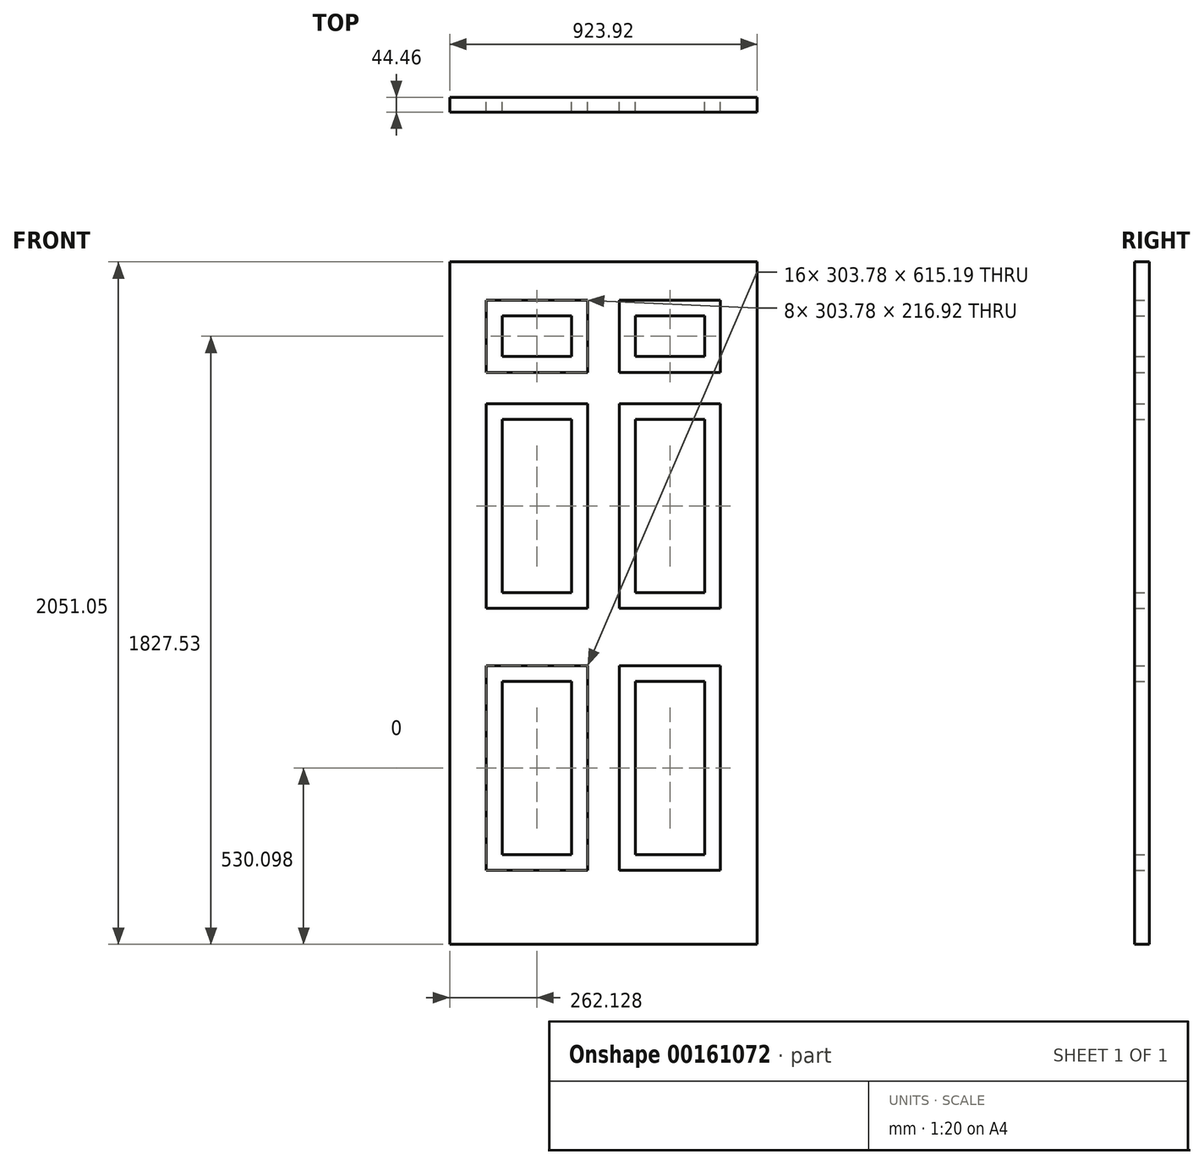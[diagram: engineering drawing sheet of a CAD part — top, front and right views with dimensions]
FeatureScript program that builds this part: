
annotation { "Feature Type Name" : "Feature", "Feature Type Description" : "" }
export const myFeature = defineFeature(function(context is Context, id is Id, definition is map)
    precondition{}
    {
        {
            var Q0;
            Q0=qCreatedBy(makeId("Front.planeOp"),FACE);
            var sketch = newSketch(context, id + "F0", { "sketchPlane" : qUnion([Q0])});
            skLineSegment(sketch, "E0.bottom", {"start": v(0, 0) * mm, "end": v(923.93, 0) * mm});
            skLineSegment(sketch, "E0.top", {"start": v(0, 2051.05) * mm, "end": v(923.92, 2051.05) * mm});
            skLineSegment(sketch, "E0.left", {"start": v(0, 0) * mm, "end": v(0, 2051.05) * mm});
            skLineSegment(sketch, "E0.right", {"start": v(923.93, 0) * mm, "end": v(923.92, 2051.05) * mm});
            skLineSegment(sketch, "E1.bottom", {"start": v(110.24, 222.5) * mm, "end": v(414.02, 222.5) * mm});
            skLineSegment(sketch, "E1.top", {"start": v(110.24, 837.7) * mm, "end": v(414.02, 837.7) * mm});
            skLineSegment(sketch, "E1.left", {"start": v(110.24, 222.5) * mm, "end": v(110.24, 837.7) * mm});
            skLineSegment(sketch, "E1.right", {"start": v(414.02, 222.5) * mm, "end": v(414.02, 837.7) * mm});
            skLineSegment(sketch, "E2.bottom", {"start": v(509.9, 222.5) * mm, "end": v(813.69, 222.5) * mm});
            skLineSegment(sketch, "E2.top", {"start": v(509.9, 837.7) * mm, "end": v(813.69, 837.7) * mm});
            skLineSegment(sketch, "E2.left", {"start": v(509.9, 222.5) * mm, "end": v(509.9, 837.7) * mm});
            skLineSegment(sketch, "E2.right", {"start": v(813.69, 222.5) * mm, "end": v(813.69, 837.7) * mm});
            skLineSegment(sketch, "E3.bottom", {"start": v(414.02, 1009.65) * mm, "end": v(110.24, 1009.65) * mm});
            skLineSegment(sketch, "E3.top", {"start": v(414.02, 1624.84) * mm, "end": v(110.24, 1624.84) * mm});
            skLineSegment(sketch, "E3.left", {"start": v(414.02, 1009.65) * mm, "end": v(414.02, 1624.84) * mm});
            skLineSegment(sketch, "E3.right", {"start": v(110.24, 1009.65) * mm, "end": v(110.24, 1624.84) * mm});
            skLineSegment(sketch, "E4.bottom", {"start": v(110.24, 1719.07) * mm, "end": v(414.02, 1719.07) * mm});
            skLineSegment(sketch, "E4.top", {"start": v(110.24, 1935.99) * mm, "end": v(414.02, 1935.99) * mm});
            skLineSegment(sketch, "E4.left", {"start": v(110.24, 1719.07) * mm, "end": v(110.24, 1935.99) * mm});
            skLineSegment(sketch, "E4.right", {"start": v(414.02, 1719.07) * mm, "end": v(414.02, 1935.99) * mm});
            skLineSegment(sketch, "E5.bottom", {"start": v(509.9, 1009.65) * mm, "end": v(813.69, 1009.65) * mm});
            skLineSegment(sketch, "E5.top", {"start": v(509.9, 1624.84) * mm, "end": v(813.69, 1624.84) * mm});
            skLineSegment(sketch, "E5.left", {"start": v(509.9, 1009.65) * mm, "end": v(509.9, 1624.84) * mm});
            skLineSegment(sketch, "E5.right", {"start": v(813.69, 1009.65) * mm, "end": v(813.69, 1624.84) * mm});
            skLineSegment(sketch, "E6.bottom", {"start": v(509.9, 1719.07) * mm, "end": v(813.69, 1719.07) * mm});
            skLineSegment(sketch, "E6.top", {"start": v(509.9, 1935.99) * mm, "end": v(813.69, 1935.99) * mm});
            skLineSegment(sketch, "E6.left", {"start": v(509.9, 1719.07) * mm, "end": v(509.9, 1935.99) * mm});
            skLineSegment(sketch, "E6.right", {"start": v(813.69, 1719.07) * mm, "end": v(813.69, 1935.99) * mm});
            skLineSegment(sketch, "E7.0", {"start": v(157.73, 1888.5) * mm, "end": v(366.52, 1888.5) * mm});
            skLineSegment(sketch, "E7.1", {"start": v(157.73, 1766.57) * mm, "end": v(157.73, 1888.5) * mm});
            skLineSegment(sketch, "E7.2", {"start": v(157.73, 1766.57) * mm, "end": v(366.52, 1766.57) * mm});
            skLineSegment(sketch, "E7.3", {"start": v(366.52, 1766.57) * mm, "end": v(366.52, 1888.5) * mm});
            skLineSegment(sketch, "E8.0", {"start": v(557.4, 1888.5) * mm, "end": v(766.2, 1888.5) * mm});
            skLineSegment(sketch, "E8.1", {"start": v(557.4, 1766.57) * mm, "end": v(557.4, 1888.5) * mm});
            skLineSegment(sketch, "E8.2", {"start": v(557.4, 1766.57) * mm, "end": v(766.2, 1766.57) * mm});
            skLineSegment(sketch, "E8.3", {"start": v(766.2, 1766.57) * mm, "end": v(766.2, 1888.5) * mm});
            skLineSegment(sketch, "E9.0", {"start": v(366.52, 1577.34) * mm, "end": v(157.73, 1577.34) * mm});
            skLineSegment(sketch, "E9.1", {"start": v(366.52, 1057.15) * mm, "end": v(366.52, 1577.34) * mm});
            skLineSegment(sketch, "E9.2", {"start": v(366.52, 1057.15) * mm, "end": v(157.73, 1057.15) * mm});
            skLineSegment(sketch, "E9.3", {"start": v(157.73, 1057.15) * mm, "end": v(157.73, 1577.34) * mm});
            skLineSegment(sketch, "E10.0", {"start": v(557.4, 1057.15) * mm, "end": v(557.4, 1577.34) * mm});
            skLineSegment(sketch, "E10.1", {"start": v(557.4, 1057.15) * mm, "end": v(766.2, 1057.15) * mm});
            skLineSegment(sketch, "E10.2", {"start": v(766.2, 1057.15) * mm, "end": v(766.2, 1577.34) * mm});
            skLineSegment(sketch, "E10.3", {"start": v(557.4, 1577.34) * mm, "end": v(766.2, 1577.34) * mm});
            skLineSegment(sketch, "E11.0", {"start": v(157.73, 790.2) * mm, "end": v(366.52, 790.2) * mm});
            skLineSegment(sketch, "E11.1", {"start": v(157.73, 270) * mm, "end": v(157.73, 790.2) * mm});
            skLineSegment(sketch, "E11.2", {"start": v(157.73, 270) * mm, "end": v(366.52, 270) * mm});
            skLineSegment(sketch, "E11.3", {"start": v(366.52, 270) * mm, "end": v(366.52, 790.2) * mm});
            skLineSegment(sketch, "E12.0", {"start": v(557.4, 790.2) * mm, "end": v(766.2, 790.2) * mm});
            skLineSegment(sketch, "E12.1", {"start": v(557.4, 270) * mm, "end": v(557.4, 790.2) * mm});
            skLineSegment(sketch, "E12.2", {"start": v(557.4, 270) * mm, "end": v(766.2, 270) * mm});
            skLineSegment(sketch, "E12.3", {"start": v(766.2, 270) * mm, "end": v(766.2, 790.2) * mm});
            skSolve(sketch);
        }
        {
            var Q0;
            Q0 = qSketchRegion(id + "F0", true);
            extrude(context, id + "F1", {"entities" : qUnion([Q0]), "depth" : 22.22 * mm, "hasSecondDirection" : true, "secondDirectionOppositeDirection" : true, "secondDirectionDepth" : 22.22 * mm});
        }
        {
            var Q0;
            Q0=qCreatedBy(makeId("Front.planeOp"),FACE);
            var sketch = newSketch(context, id + "F2", { "sketchPlane" : qUnion([Q0])});
            skLineSegment(sketch, "E13.0.0", {"start": v(366.52, 1888.5) * mm, "end": v(157.73, 1888.5) * mm});
            skLineSegment(sketch, "E13.0.1", {"start": v(157.73, 1888.5) * mm, "end": v(157.73, 1766.57) * mm});
            skLineSegment(sketch, "E13.0.2", {"start": v(157.73, 1766.57) * mm, "end": v(366.52, 1766.57) * mm});
            skLineSegment(sketch, "E13.0.3", {"start": v(366.52, 1766.57) * mm, "end": v(366.52, 1888.5) * mm});
            skLineSegment(sketch, "E14.0.0", {"start": v(766.2, 1888.5) * mm, "end": v(557.4, 1888.5) * mm});
            skLineSegment(sketch, "E14.0.1", {"start": v(557.4, 1888.5) * mm, "end": v(557.4, 1766.57) * mm});
            skLineSegment(sketch, "E14.0.2", {"start": v(557.4, 1766.57) * mm, "end": v(766.2, 1766.57) * mm});
            skLineSegment(sketch, "E14.0.3", {"start": v(766.2, 1766.57) * mm, "end": v(766.2, 1888.5) * mm});
            skLineSegment(sketch, "E15.0.0", {"start": v(557.4, 1577.34) * mm, "end": v(557.4, 1057.15) * mm});
            skLineSegment(sketch, "E15.0.1", {"start": v(557.4, 1057.15) * mm, "end": v(766.2, 1057.15) * mm});
            skLineSegment(sketch, "E15.0.2", {"start": v(766.2, 1057.15) * mm, "end": v(766.2, 1577.34) * mm});
            skLineSegment(sketch, "E15.0.3", {"start": v(766.2, 1577.34) * mm, "end": v(557.4, 1577.34) * mm});
            skLineSegment(sketch, "E16.0.0", {"start": v(366.52, 1057.15) * mm, "end": v(366.52, 1577.34) * mm});
            skLineSegment(sketch, "E16.0.1", {"start": v(366.52, 1577.34) * mm, "end": v(157.73, 1577.34) * mm});
            skLineSegment(sketch, "E16.0.2", {"start": v(157.73, 1577.34) * mm, "end": v(157.73, 1057.15) * mm});
            skLineSegment(sketch, "E16.0.3", {"start": v(157.73, 1057.15) * mm, "end": v(366.52, 1057.15) * mm});
            skLineSegment(sketch, "E17.0.0", {"start": v(366.52, 790.2) * mm, "end": v(157.73, 790.2) * mm});
            skLineSegment(sketch, "E17.0.1", {"start": v(157.73, 790.2) * mm, "end": v(157.73, 270) * mm});
            skLineSegment(sketch, "E17.0.2", {"start": v(157.73, 270) * mm, "end": v(366.52, 270) * mm});
            skLineSegment(sketch, "E17.0.3", {"start": v(366.52, 270) * mm, "end": v(366.52, 790.2) * mm});
            skLineSegment(sketch, "E18.0.0", {"start": v(766.2, 790.2) * mm, "end": v(557.4, 790.2) * mm});
            skLineSegment(sketch, "E18.0.1", {"start": v(557.4, 790.2) * mm, "end": v(557.4, 270) * mm});
            skLineSegment(sketch, "E18.0.2", {"start": v(557.4, 270) * mm, "end": v(766.2, 270) * mm});
            skLineSegment(sketch, "E18.0.3", {"start": v(766.2, 270) * mm, "end": v(766.2, 790.2) * mm});
            skSolve(sketch);
        }
        {
            var Q0;
            Q0 = qSketchRegion(id + "F2", true);
            var Q1;
            Q1=makeQuery(id+"F1.opExtrude","CAP_FACE",FACE,{"disambiguationData":[OSD([sQuery(id+"F0.wireOp",EDGE,"E0.bottom"),sQuery(id+"F0.wireOp",EDGE,"E0.top"),sQuery(id+"F0.wireOp",EDGE,"E0.left"),sQuery(id+"F0.wireOp",EDGE,"E0.right"),sQuery(id+"F0.wireOp",EDGE,"E1.bottom"),sQuery(id+"F0.wireOp",EDGE,"E1.top"),sQuery(id+"F0.wireOp",EDGE,"E1.left"),sQuery(id+"F0.wireOp",EDGE,"E1.right"),sQuery(id+"F0.wireOp",EDGE,"E2.bottom"),sQuery(id+"F0.wireOp",EDGE,"E2.top"),sQuery(id+"F0.wireOp",EDGE,"E2.left"),sQuery(id+"F0.wireOp",EDGE,"E2.right"),sQuery(id+"F0.wireOp",EDGE,"E3.bottom"),sQuery(id+"F0.wireOp",EDGE,"E3.top"),sQuery(id+"F0.wireOp",EDGE,"E3.left"),sQuery(id+"F0.wireOp",EDGE,"E3.right"),sQuery(id+"F0.wireOp",EDGE,"E4.bottom"),sQuery(id+"F0.wireOp",EDGE,"E4.top"),sQuery(id+"F0.wireOp",EDGE,"E4.left"),sQuery(id+"F0.wireOp",EDGE,"E4.right"),sQuery(id+"F0.wireOp",EDGE,"E5.bottom"),sQuery(id+"F0.wireOp",EDGE,"E5.top"),sQuery(id+"F0.wireOp",EDGE,"E5.left"),sQuery(id+"F0.wireOp",EDGE,"E5.right"),sQuery(id+"F0.wireOp",EDGE,"E6.bottom"),sQuery(id+"F0.wireOp",EDGE,"E6.top"),sQuery(id+"F0.wireOp",EDGE,"E6.left"),sQuery(id+"F0.wireOp",EDGE,"E6.right")])],"isStart":false});
            var Q2;
            Q2=makeQuery(id+"F1.opExtrude","CAP_FACE",FACE,{"disambiguationData":[OSD([sQuery(id+"F0.wireOp",EDGE,"E0.bottom"),sQuery(id+"F0.wireOp",EDGE,"E0.top"),sQuery(id+"F0.wireOp",EDGE,"E0.left"),sQuery(id+"F0.wireOp",EDGE,"E0.right"),sQuery(id+"F0.wireOp",EDGE,"E1.bottom"),sQuery(id+"F0.wireOp",EDGE,"E1.top"),sQuery(id+"F0.wireOp",EDGE,"E1.left"),sQuery(id+"F0.wireOp",EDGE,"E1.right"),sQuery(id+"F0.wireOp",EDGE,"E2.bottom"),sQuery(id+"F0.wireOp",EDGE,"E2.top"),sQuery(id+"F0.wireOp",EDGE,"E2.left"),sQuery(id+"F0.wireOp",EDGE,"E2.right"),sQuery(id+"F0.wireOp",EDGE,"E3.bottom"),sQuery(id+"F0.wireOp",EDGE,"E3.top"),sQuery(id+"F0.wireOp",EDGE,"E3.left"),sQuery(id+"F0.wireOp",EDGE,"E3.right"),sQuery(id+"F0.wireOp",EDGE,"E4.bottom"),sQuery(id+"F0.wireOp",EDGE,"E4.top"),sQuery(id+"F0.wireOp",EDGE,"E4.left"),sQuery(id+"F0.wireOp",EDGE,"E4.right"),sQuery(id+"F0.wireOp",EDGE,"E5.bottom"),sQuery(id+"F0.wireOp",EDGE,"E5.top"),sQuery(id+"F0.wireOp",EDGE,"E5.left"),sQuery(id+"F0.wireOp",EDGE,"E5.right"),sQuery(id+"F0.wireOp",EDGE,"E6.bottom"),sQuery(id+"F0.wireOp",EDGE,"E6.top"),sQuery(id+"F0.wireOp",EDGE,"E6.left"),sQuery(id+"F0.wireOp",EDGE,"E6.right")])],"isStart":true});
            extrude(context, id + "F3", {"entities" : qUnion([Q0]), "endBound" : BoundingType.UP_TO_SURFACE, "endBoundEntityFace" : qUnion([Q1]), "depth" : 25.4 * mm, "hasSecondDirection" : true, "secondDirectionBound" : SecondDirectionBoundingType.UP_TO_SURFACE, "secondDirectionOppositeDirection" : true, "secondDirectionBoundEntityFace" : qUnion([Q2]), "secondDirectionDepth" : 25.4 * mm});
        }
    });
